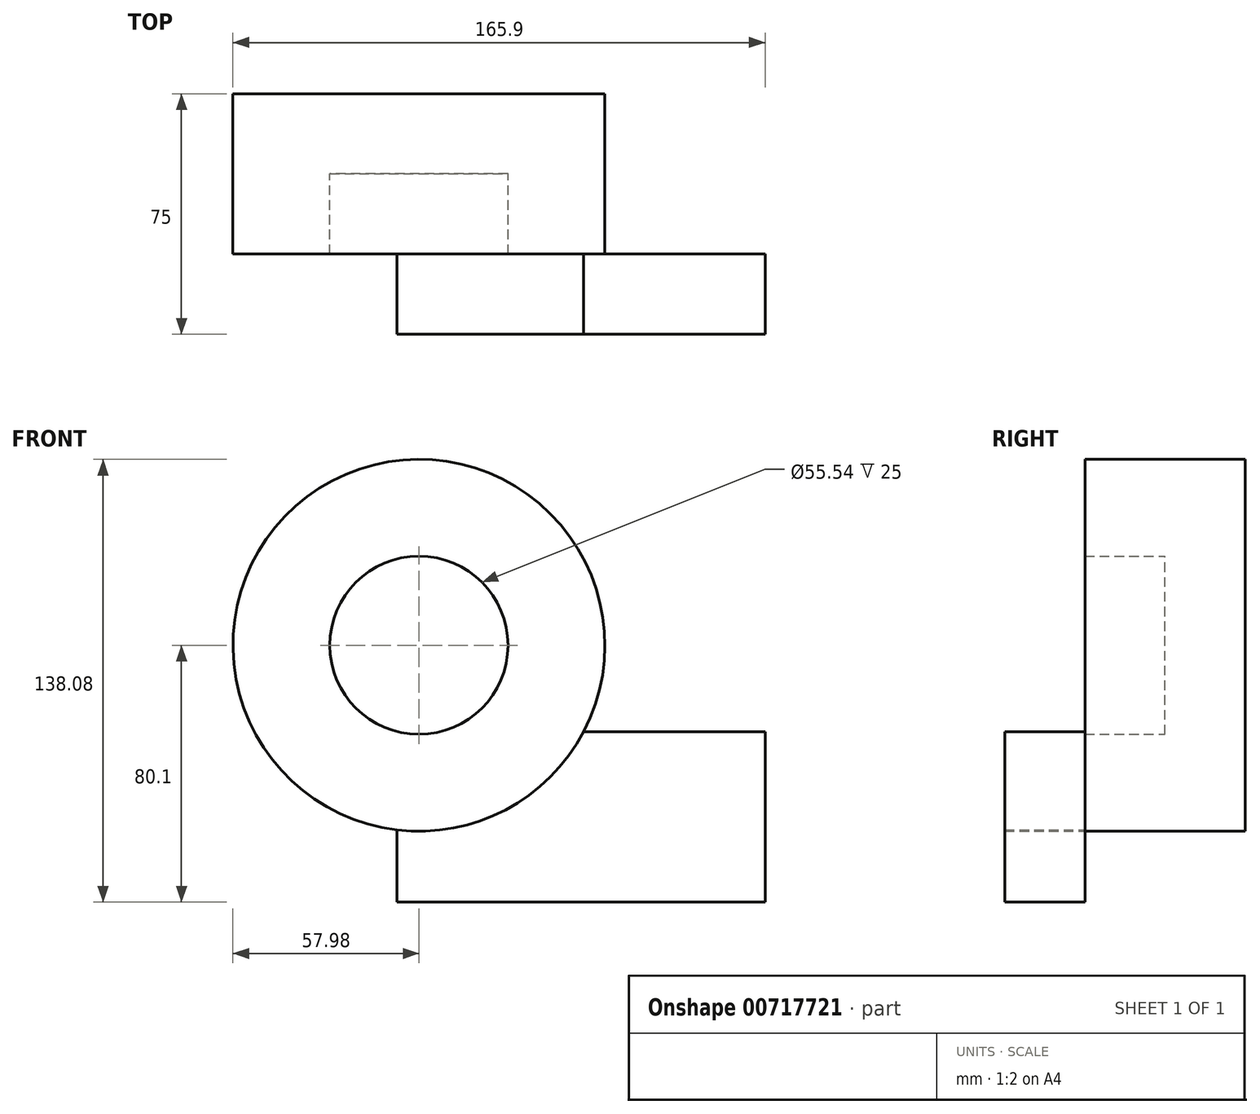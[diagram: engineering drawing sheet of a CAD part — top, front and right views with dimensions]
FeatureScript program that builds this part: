
annotation { "Feature Type Name" : "Feature", "Feature Type Description" : "" }
export const myFeature = defineFeature(function(context is Context, id is Id, definition is map)
    precondition{}
    {
        {
            var Q0;
            Q0=qCreatedBy(makeId("Front.planeOp"),FACE);
            var sketch = newSketch(context, id + "F0", { "sketchPlane" : qUnion([Q0])});
            skCircle(sketch, "E0", {"center": v(0, 0) * mm, "radius": 27.77 * mm});
            skCircle(sketch, "E1", {"center": v(0, 0) * mm, "radius": 57.98 * mm});
            skSolve(sketch);
        }
        {
            var Q0;
            Q0=makeQuery(id+"F0.imprint","IMPRINT",FACE,{"disambiguationData":[TD([[makeQuery(id+"F0.imprint","IMPRINT",EDGE,{"derivedFrom":sQuery(id+"F0.wireOp",EDGE,"E0")}),1.0]])]});
            extrude(context, id + "F1", {"entities" : qUnion([Q0]), "depth" : 25 * mm, "offsetDistance" : 25 * mm});
        }
        {
            var Q0;
            Q0=makeQuery(id+"F0.imprint","IMPRINT",FACE,{"disambiguationData":[TD([[makeQuery(id+"F0.imprint","IMPRINT",EDGE,{"derivedFrom":sQuery(id+"F0.wireOp",EDGE,"E0")}),-1.0]])]});
            extrude(context, id + "F2", {"entities" : qUnion([Q0]), "operationType" : NewBodyOperationType.ADD, "depth" : 50 * mm, "offsetDistance" : 25 * mm});
        }
        {
            var Q0;
            Q0=makeQuery(id+"F2.opExtrude","CAP_FACE",FACE,{"disambiguationData":[OSD([sQuery(id+"F0.wireOp",EDGE,"E0"),sQuery(id+"F0.wireOp",EDGE,"E1")])],"isStart":false});
            var sketch = newSketch(context, id + "F3", { "sketchPlane" : qUnion([Q0])});
            skLineSegment(sketch, "E2.bottom", {"start": v(-6.86, -26.9) * mm, "end": v(107.92, -26.9) * mm});
            skLineSegment(sketch, "E2.top", {"start": v(-6.86, -80.1) * mm, "end": v(107.92, -80.1) * mm});
            skLineSegment(sketch, "E2.left", {"start": v(-6.86, -26.9) * mm, "end": v(-6.86, -80.1) * mm});
            skLineSegment(sketch, "E2.right", {"start": v(107.92, -26.9) * mm, "end": v(107.92, -80.1) * mm});
            skSolve(sketch);
        }
        {
            var Q0;
            {var subQ2=sQuery(id+"F3.wireOp",EDGE,"E2.top");Q0=makeQuery(id+"F3.imprint","IMPRINT",FACE,{"disambiguationData":[TD([[makeQuery(id+"F3.imprint","IMPRINT",EDGE,{"derivedFrom":subQ2}),1.0]])]});}
            extrude(context, id + "F4", {"entities" : qUnion([Q0]), "operationType" : NewBodyOperationType.ADD, "depth" : 25 * mm, "offsetDistance" : 25 * mm});
        }
    });
